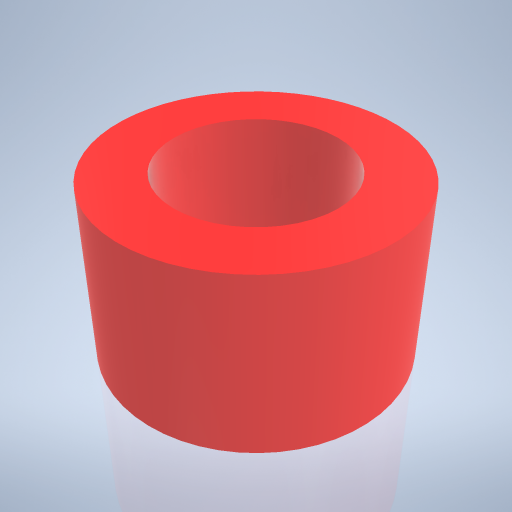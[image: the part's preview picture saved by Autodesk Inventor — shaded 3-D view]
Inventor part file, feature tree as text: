
AUTODESK INVENTOR PART (.ipt)
format: ipt  version: 2024.2 (Build 282272000, 272)  size: 217,600 bytes
history: native  units: mm
features: sketch x2, extrude x1, hole x1
ambient origin geometry x8: Origin, YZ Plane, XZ Plane, XY Plane, X Axis, Y Axis, Z Axis, Center Point
bodies: Volumenkörper1 (feature_tree)
feature tree (4):
  extrude  "Extrusion1"  Depth=3.0mm TaperAngle=0.0deg
  hole  "Bohrung1"  [1 undecoded]
  sketch  "Skizze1"  dims[d0=5.0mm d1=3.0mm d2=0.0mm]
  sketch  "Skizze2"  dims[d3=3.0mm d4=6.0mm d5=8.4mm d6=2.0mm d7=90.0deg d8=8.0mm d9=0.0mm]
note: 1 required parameter value undecoded (feature->parameter linkage not recoverable at this tier; creation-order binding heuristic only, values carry confidence <= 0.55)
